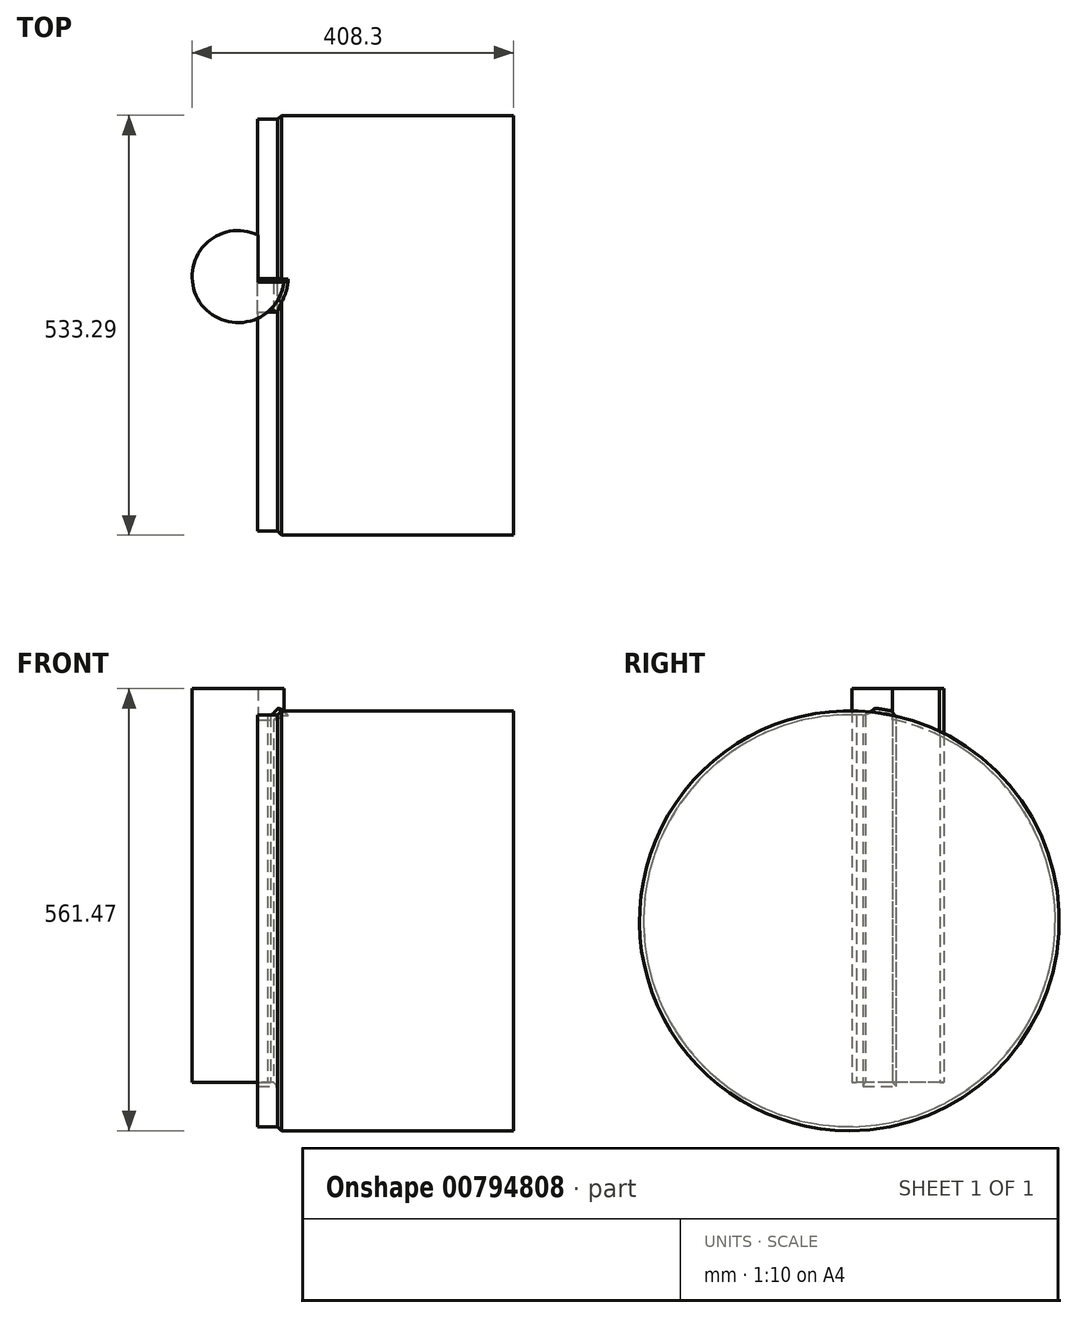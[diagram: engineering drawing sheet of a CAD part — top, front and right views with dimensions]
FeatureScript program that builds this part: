
annotation { "Feature Type Name" : "Feature", "Feature Type Description" : "" }
export const myFeature = defineFeature(function(context is Context, id is Id, definition is map)
    precondition{}
    {
        {
            var Q0;
            Q0=qCreatedBy(makeId("Top.planeOp"),FACE);
            var sketch = newSketch(context, id + "F0", { "sketchPlane" : qUnion([Q0])});
            skLineSegment(sketch, "E0.bottom", {"start": v(24.48, 37.69) * mm, "end": v(-24.65, 37.69) * mm});
            skLineSegment(sketch, "E0.top", {"start": v(24.48, -28.09) * mm, "end": v(-24.65, -28.09) * mm});
            skLineSegment(sketch, "E0.left", {"start": v(24.48, 37.69) * mm, "end": v(24.48, -28.09) * mm});
            skLineSegment(sketch, "E0.right", {"start": v(-24.65, 37.69) * mm, "end": v(-24.65, -28.09) * mm});
            skCircle(sketch, "E1", {"center": v(-49.82, -20.8) * mm, "radius": 58.48 * mm});
            skSolve(sketch);
        }
        {
            var Q0;
            {var subQ0=sQuery(id+"F0.wireOp",EDGE,"E0.right");var subQ1=sQuery(id+"F0.wireOp",EDGE,"E0.top");var subQ2=makeQuery(id+"F0.imprint","INTERSECT",VERTEX,{"derivedFrom":[subQ1,subQ0]});Q0=makeQuery(id+"F0.imprint","IMPRINT",FACE,{"disambiguationData":[TD([[makeQuery(id+"F0.imprint","IMPRINT",EDGE,{"disambiguationData":[TD([[subQ2,1.0]])],"derivedFrom":subQ1}),1.0]])]});}
            extrude(context, id + "F1", {"entities" : qUnion([Q0]), "depth" : 500 * mm, "offsetDistance" : 25 * mm});
        }
        {
            var Q0;
            Q0=qCreatedBy(makeId("Right.planeOp"),FACE);
            var sketch = newSketch(context, id + "F2", { "sketchPlane" : qUnion([Q0])});
            skCircle(sketch, "E2", {"center": v(-82.67, 205.17) * mm, "radius": 266.64 * mm});
            skSolve(sketch);
        }
        {
            var Q0;
            Q0 = qSketchRegion(id + "F2", true);
            extrude(context, id + "F3", {"entities" : qUnion([Q0]), "operationType" : NewBodyOperationType.ADD, "depth" : 300 * mm, "offsetDistance" : 25 * mm});
        }
        {
            var Q0;
            Q0=makeQuery(id+"F3.opExtrude","CAP_FACE",FACE,{"disambiguationData":[OSD([sQuery(id+"F2.wireOp",EDGE,"E2")])],"isStart":true});
            chamfer(context, id + "F4", {"entities" : qUnion([Q0]), "width" : 5 * mm, "tangentPropagation" : true});
        }
        {
            var Q0;
            Q0=makeQuery(id+"F3.opExtrude","CAP_FACE",FACE,{"disambiguationData":[OSD([sQuery(id+"F2.wireOp",EDGE,"E2")])],"isStart":true});
            var sketch = newSketch(context, id + "F5", { "sketchPlane" : qUnion([Q0])});
            skSolve(sketch);
        }
        {
            var Q0;
            {var subQ0=sQuery(id+"F2.wireOp",EDGE,"E2");var subQ1=makeQuery(id+"F3.opExtrude","CAP_FACE",FACE,{"disambiguationData":[OSD([subQ0])],"isStart":true});var subQ2=subQ1;Q0=makeQuery(id+"F5.imprint","IMPRINT",FACE,{"disambiguationData":[TD([[makeQuery(id+"F5.imprint","IMPRINT",EDGE,{"derivedFrom":makeQuery(id+"F4.opChamfer","BLEND_EDGE",EDGE,{"blendedFrom":[makeQuery(id+"F3.opExtrude","CAP_EDGE",EDGE,{"disambiguationData":[OSD([subQ0])],"isStart":true}),subQ2],"blendedInto":[subQ2]})}),1.0]])]});}
            extrude(context, id + "F6", {"entities" : qUnion([Q0]), "operationType" : NewBodyOperationType.ADD, "depth" : 25 * mm, "offsetDistance" : 25 * mm});
        }
    });
